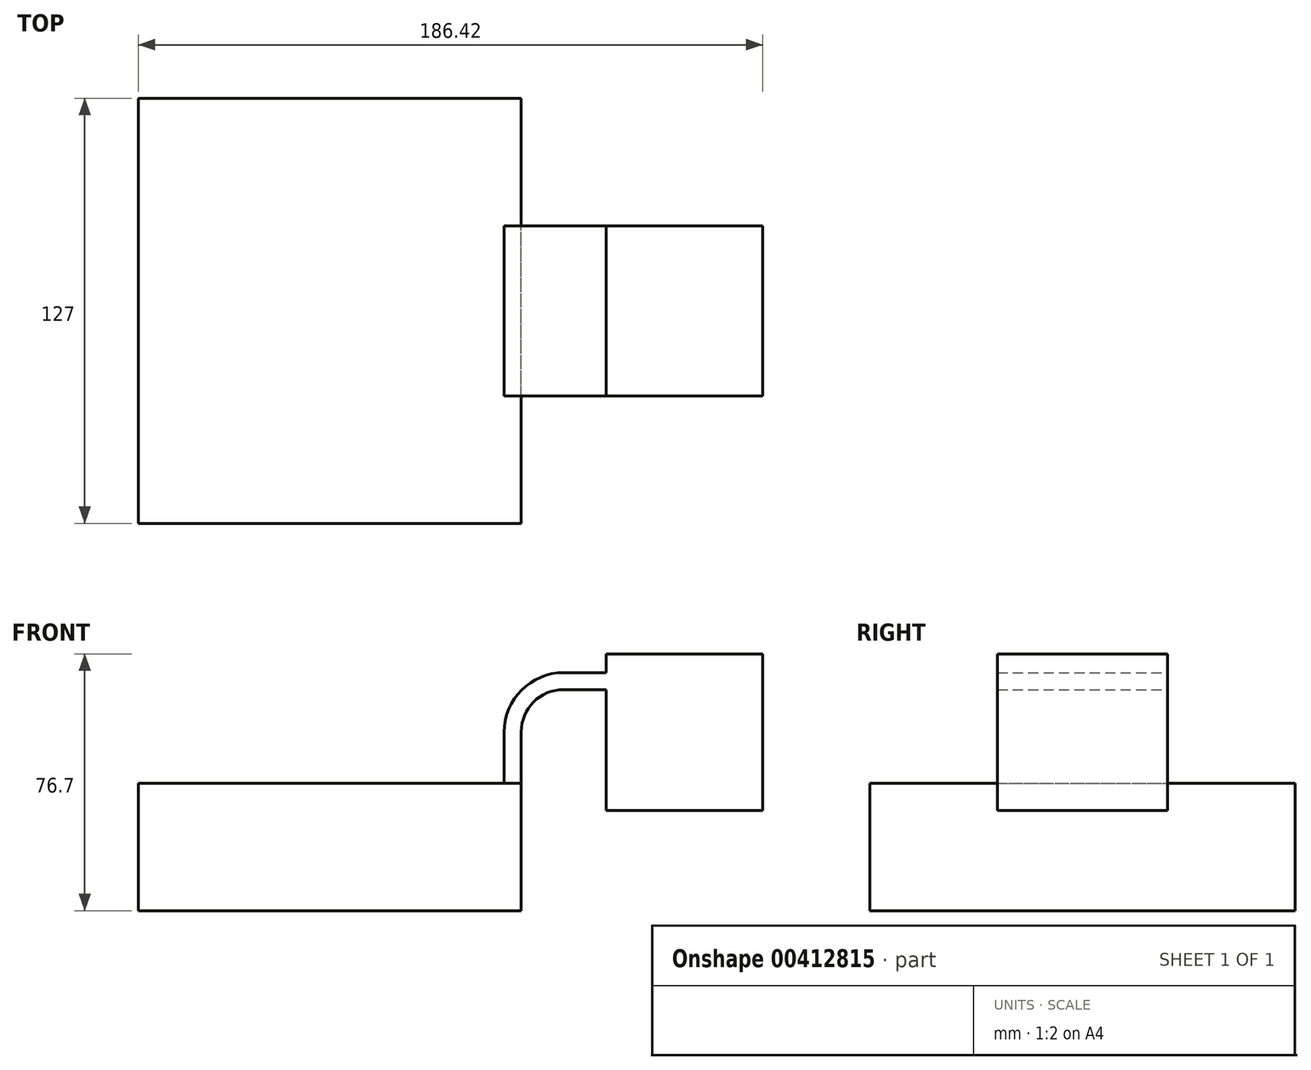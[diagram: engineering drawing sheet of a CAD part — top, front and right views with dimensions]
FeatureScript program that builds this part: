
annotation { "Feature Type Name" : "Feature", "Feature Type Description" : "" }
export const myFeature = defineFeature(function(context is Context, id is Id, definition is map)
    precondition{}
    {
        {
            var Q0;
            Q0=qCreatedBy(makeId("Front.planeOp"),FACE);
            var sketch = newSketch(context, id + "F0", { "sketchPlane" : qUnion([Q0])});
            skLineSegment(sketch, "E0.bottom", {"start": v(57.15, 19.05) * mm, "end": v(-57.15, 19.05) * mm});
            skLineSegment(sketch, "E0.top", {"start": v(57.15, -19.05) * mm, "end": v(-57.15, -19.05) * mm});
            skLineSegment(sketch, "E0.left", {"start": v(57.15, 19.05) * mm, "end": v(57.15, -19.05) * mm});
            skLineSegment(sketch, "E0.right", {"start": v(-57.15, 19.05) * mm, "end": v(-57.15, -19.05) * mm});
            skPoint(sketch, "E0.middle", {"position": v(0, 0) * mm});
            skLineSegment(sketch, "E1.bottom", {"start": v(82.55, 57.65) * mm, "end": v(129.27, 57.65) * mm});
            skLineSegment(sketch, "E1.top", {"start": v(82.55, 10.93) * mm, "end": v(129.27, 10.93) * mm});
            skLineSegment(sketch, "E1.left", {"start": v(82.55, 57.65) * mm, "end": v(82.55, 10.93) * mm});
            skLineSegment(sketch, "E1.right", {"start": v(129.27, 57.65) * mm, "end": v(129.27, 10.93) * mm});
            skLineSegment(sketch, "E2", {"start": v(57.15, 19.05) * mm, "end": v(57.15, 34.3) * mm});
            skPoint(sketch, "E2.endSnap0", {"position": v(82.55, 34.3) * mm});
            skArc(sketch, "E3", {"start": v(57.15, 34.3) * mm, "mid": v(60.87, 43.27) * mm, "end": v(69.85, 47) * mm});
            skLineSegment(sketch, "E4", {"start": v(69.85, 47) * mm, "end": v(82.55, 47) * mm});
            skLineSegment(sketch, "E5.0", {"start": v(69.85, 52.07) * mm, "end": v(95.25, 52.07) * mm});
            skArc(sketch, "E5.1", {"start": v(52.07, 34.3) * mm, "mid": v(57.28, 46.86) * mm, "end": v(69.85, 52.07) * mm});
            skLineSegment(sketch, "E5.2", {"start": v(52.07, 8.9) * mm, "end": v(52.07, 34.3) * mm});
            skFitSpline(sketch, "E6", {"points": [v(-57.15, 19.05) * mm, v(69.85, 52.07) * mm], "startDerivative": vector(15, 84.12) * mm, "endDerivative": vector(138.33, -5.35) * mm});
            skSolve(sketch);
        }
        {
            var Q0;
            Q0=makeQuery(id+"F0.imprint","IMPRINT",FACE,{"disambiguationData":[TD([[makeQuery(id+"F0.imprint","IMPRINT",EDGE,{"derivedFrom":sQuery(id+"F0.wireOp",EDGE,"E0.top")}),-1.0]])]});
            extrude(context, id + "F1", {"entities" : qUnion([Q0]), "endBound" : BoundingType.SYMMETRIC, "depth" : 127 * mm});
        }
        {
            var Q0;
            Q0=makeQuery(id+"F0.imprint","IMPRINT",FACE,{"disambiguationData":[TD([[makeQuery(id+"F0.imprint","IMPRINT",EDGE,{"derivedFrom":sQuery(id+"F0.wireOp",EDGE,"E5.1")}),1.0]])]});
            extrude(context, id + "F2", {"entities" : qUnion([Q0]), "operationType" : NewBodyOperationType.ADD, "endBound" : BoundingType.SYMMETRIC, "depth" : 25.4 * mm});
        }
        {
            var Q0;
            {var subQ3=sQuery(id+"F0.wireOp",EDGE,"E1.bottom");Q0=makeQuery(id+"F0.imprint","IMPRINT",FACE,{"disambiguationData":[TD([[makeQuery(id+"F0.imprint","IMPRINT",EDGE,{"derivedFrom":subQ3}),-1.0]])]});}
            var Q1;
            {var subQ0=sQuery(id+"F0.wireOp",EDGE,"E2");Q1=makeQuery(id+"F0.imprint","IMPRINT",FACE,{"disambiguationData":[TD([[makeQuery(id+"F0.imprint","IMPRINT",EDGE,{"derivedFrom":subQ0}),1.0]])]});}
            extrude(context, id + "F3", {"entities" : qUnion([Q0, Q1]), "operationType" : NewBodyOperationType.ADD, "endBound" : BoundingType.SYMMETRIC, "depth" : 50.8 * mm});
        }
    });
